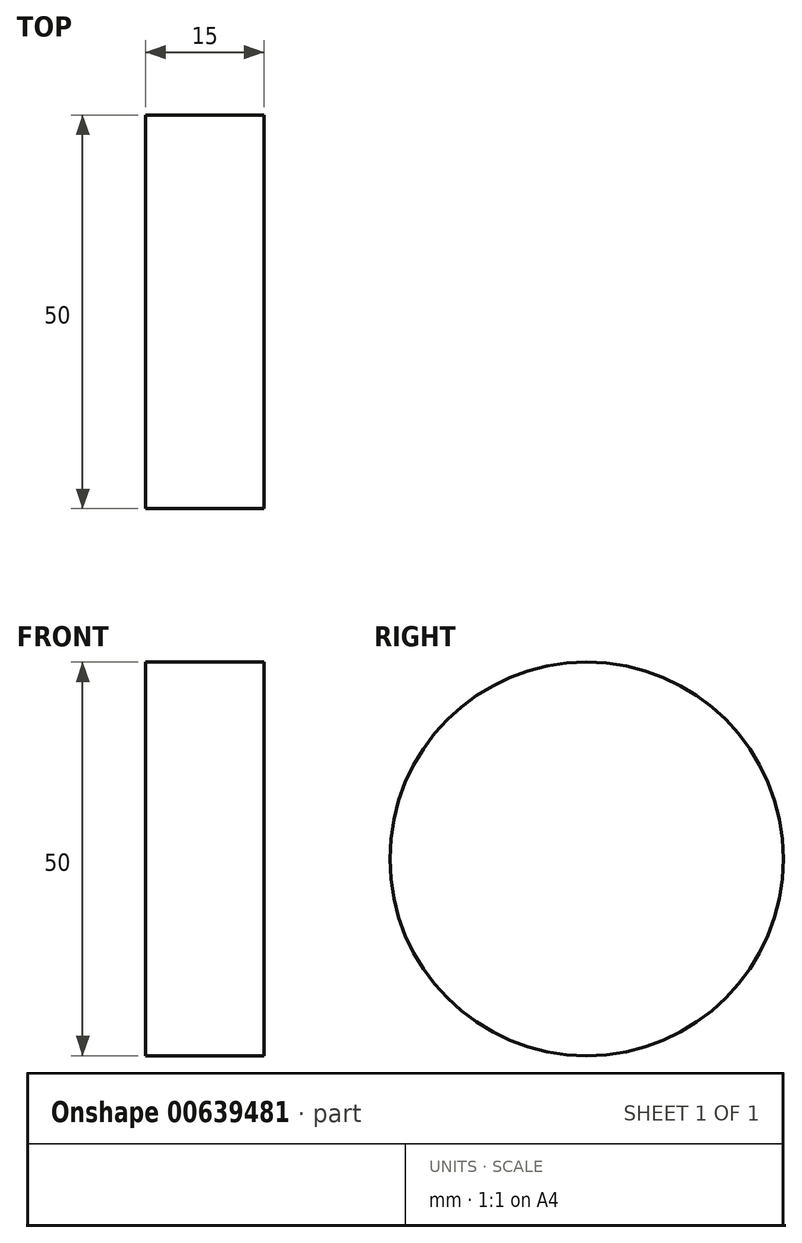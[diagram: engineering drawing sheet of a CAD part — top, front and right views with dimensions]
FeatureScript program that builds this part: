
annotation { "Feature Type Name" : "Feature", "Feature Type Description" : "" }
export const myFeature = defineFeature(function(context is Context, id is Id, definition is map)
    precondition{}
    {
        {
            var Q0;
            Q0=qCreatedBy(makeId("Right.planeOp"),FACE);
            var sketch = newSketch(context, id + "F0", { "sketchPlane" : qUnion([Q0])});
            skCircle(sketch, "E0", {"center": v(0, 0) * mm, "radius": 25 * mm});
            skSolve(sketch);
        }
        {
            var Q0;
            Q0=makeQuery(id+"F0.imprint","IMPRINT",FACE,{"disambiguationData":[TD([[makeQuery(id+"F0.imprint","IMPRINT",EDGE,{"derivedFrom":sQuery(id+"F0.wireOp",EDGE,"E0")}),1.0]])]});
            extrude(context, id + "F1", {"entities" : qUnion([Q0]), "depth" : 15 * mm, "offsetDistance" : 25 * mm});
        }
    });
